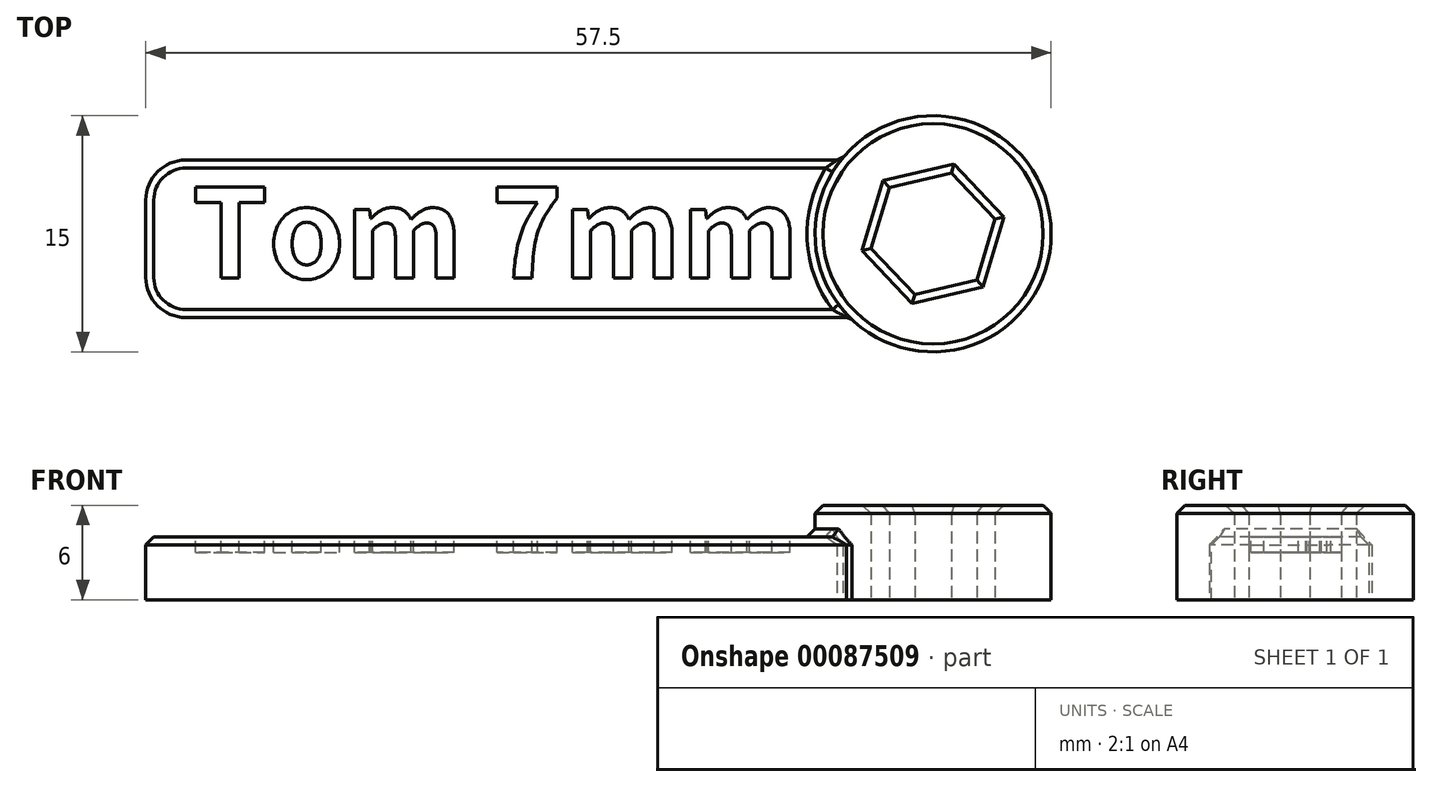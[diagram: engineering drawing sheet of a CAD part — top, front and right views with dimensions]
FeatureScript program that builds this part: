
annotation { "Feature Type Name" : "Feature", "Feature Type Description" : "" }
export const myFeature = defineFeature(function(context is Context, id is Id, definition is map)
    precondition{}
    {
        {
            var Q0;
            Q0=qCreatedBy(makeId("Top.planeOp"),FACE);
            var sketch = newSketch(context, id + "F0", { "sketchPlane" : qUnion([Q0])});
            skCircle(sketch, "E0.cCircle", {"center": v(0, 0) * mm, "radius": 4.04 * mm, "construction": true});
            skLineSegment(sketch, "E0.0", {"start": v(3.93, 0.93) * mm, "end": v(1.16, 3.87) * mm});
            skLineSegment(sketch, "E0.1", {"start": v(2.77, -2.94) * mm, "end": v(3.93, 0.93) * mm});
            skLineSegment(sketch, "E0.2", {"start": v(-1.16, -3.87) * mm, "end": v(2.77, -2.94) * mm});
            skLineSegment(sketch, "E0.3", {"start": v(-3.93, -0.93) * mm, "end": v(-1.16, -3.87) * mm});
            skLineSegment(sketch, "E0.4", {"start": v(-2.77, 2.94) * mm, "end": v(-3.93, -0.93) * mm});
            skLineSegment(sketch, "E0.5", {"start": v(1.16, 3.87) * mm, "end": v(-2.77, 2.94) * mm});
            skCircle(sketch, "E1", {"center": v(0, 0) * mm, "radius": 7.5 * mm});
            skLineSegment(sketch, "E2.bottom", {"start": v(-50, -5.32) * mm, "end": v(-5.29, -5.32) * mm});
            skLineSegment(sketch, "E2.top", {"start": v(-50, 4.68) * mm, "end": v(-5.86, 4.68) * mm});
            skLineSegment(sketch, "E2.left", {"start": v(-50, -5.32) * mm, "end": v(-50, 4.68) * mm});
            skSolve(sketch);
        }
        {
            var Q0;
            Q0=makeQuery(id+"F0.imprint","IMPRINT",FACE,{"disambiguationData":[TD([[makeQuery(id+"F0.imprint","IMPRINT",EDGE,{"derivedFrom":sQuery(id+"F0.wireOp",EDGE,"E0.0")}),-1.0]])]});
            extrude(context, id + "F1", {"entities" : qUnion([Q0]), "depth" : 6 * mm});
        }
        {
            var Q0;
            {var subQ0=sQuery(id+"F0.wireOp",EDGE,"E2.bottom");Q0=makeQuery(id+"F0.imprint","IMPRINT",FACE,{"disambiguationData":[TD([[makeQuery(id+"F0.imprint","IMPRINT",EDGE,{"derivedFrom":subQ0}),1.0]])]});}
            extrude(context, id + "F2", {"entities" : qUnion([Q0]), "operationType" : NewBodyOperationType.ADD, "depth" : 4 * mm});
        }
        {
            var Q0;
            Q0=makeQuery(id+"F2.opExtrude","SWEPT_EDGE",EDGE,{"disambiguationData":[OSD([sQuery(id+"F0.wireOp",EDGE,"E2.bottom"),sQuery(id+"F0.wireOp",EDGE,"E2.left")])]});
            var Q1;
            Q1=makeQuery(id+"F2.opExtrude","SWEPT_EDGE",EDGE,{"disambiguationData":[OSD([sQuery(id+"F0.wireOp",EDGE,"E2.top"),sQuery(id+"F0.wireOp",EDGE,"E2.left")])]});
            fillet(context, id + "F3", {"entities" : qUnion([Q0, Q1]), "radius" : 2.54 * mm, "tangentPropagation" : true, "allowEdgeOverflow" : false});
        }
        {
            var Q0;
            Q0=makeQuery(id+"F1.opExtrude","CAP_FACE",FACE,{"disambiguationData":[OSD([sQuery(id+"F0.wireOp",EDGE,"E0.0"),sQuery(id+"F0.wireOp",EDGE,"E0.1"),sQuery(id+"F0.wireOp",EDGE,"E0.2"),sQuery(id+"F0.wireOp",EDGE,"E0.3"),sQuery(id+"F0.wireOp",EDGE,"E0.4"),sQuery(id+"F0.wireOp",EDGE,"E0.5"),sQuery(id+"F0.wireOp",EDGE,"E1")])],"isStart":false});
            chamfer(context, id + "F4", {"entities" : qUnion([Q0]), "width" : 0.5 * mm, "tangentPropagation" : true});
        }
        {
            var Q0;
            Q0=makeQuery(id+"F2.opExtrude","CAP_FACE",FACE,{"disambiguationData":[OSD([sQuery(id+"F0.wireOp",EDGE,"E1"),sQuery(id+"F0.wireOp",EDGE,"E2.bottom"),sQuery(id+"F0.wireOp",EDGE,"E2.top"),sQuery(id+"F0.wireOp",EDGE,"E2.left")])],"isStart":false});
            chamfer(context, id + "F5", {"entities" : qUnion([Q0]), "width" : 0.5 * mm, "tangentPropagation" : true});
        }
        {
            var Q0;
            Q0=makeQuery(id+"F2.opExtrude","CAP_FACE",FACE,{"disambiguationData":[OSD([sQuery(id+"F0.wireOp",EDGE,"E1"),sQuery(id+"F0.wireOp",EDGE,"E2.bottom"),sQuery(id+"F0.wireOp",EDGE,"E2.top"),sQuery(id+"F0.wireOp",EDGE,"E2.left")])],"isStart":false});
            var sketch = newSketch(context, id + "F6", { "sketchPlane" : qUnion([Q0])});
            skText(sketch, "E3", { "text": "Tom 7mm", "fontName": "NotoSansCJKsc-Bold.otf"});
            const initialGuessF6  = {"E3": [-0.04708, -0.0028, 1, 0, 0.0056]};
            skSetInitialGuess(sketch, initialGuessF6);
            skSolve(sketch);
        }
        {
            var Q0;
            Q0=makeQuery(id+"F6.imprint","IMPRINT",FACE,{"disambiguationData":[TD([[makeQuery(id+"F6.imprint","IMPRINT",EDGE,{"derivedFrom":sQuery(id+"F6.wireOp",EDGE,"E3.sketch_text.stroke-0")}),1.0]])]});
            var Q1;
            Q1=makeQuery(id+"F6.imprint","IMPRINT",FACE,{"disambiguationData":[TD([[makeQuery(id+"F6.imprint","IMPRINT",EDGE,{"derivedFrom":sQuery(id+"F6.wireOp",EDGE,"E3.sketch_text.stroke-16")}),1.0]])]});
            var Q2;
            Q2=makeQuery(id+"F6.imprint","IMPRINT",FACE,{"disambiguationData":[TD([[makeQuery(id+"F6.imprint","IMPRINT",EDGE,{"derivedFrom":sQuery(id+"F6.wireOp",EDGE,"E3.sketch_text.stroke-36")}),1.0]])]});
            var Q3;
            Q3=makeQuery(id+"F6.imprint","IMPRINT",FACE,{"disambiguationData":[TD([[makeQuery(id+"F6.imprint","IMPRINT",EDGE,{"derivedFrom":sQuery(id+"F6.wireOp",EDGE,"E3.sketch_text.stroke-43")}),1.0]])]});
            var Q4;
            Q4=makeQuery(id+"F6.imprint","IMPRINT",FACE,{"disambiguationData":[TD([[makeQuery(id+"F6.imprint","IMPRINT",EDGE,{"derivedFrom":sQuery(id+"F6.wireOp",EDGE,"E3.sketch_text.stroke-63")}),1.0]])]});
            var Q5;
            Q5=makeQuery(id+"F6.imprint","IMPRINT",FACE,{"disambiguationData":[TD([[makeQuery(id+"F6.imprint","IMPRINT",EDGE,{"derivedFrom":sQuery(id+"F6.wireOp",EDGE,"E3.sketch_text.stroke-8")}),1.0]])]});
            extrude(context, id + "F7", {"entities" : qUnion([Q0, Q1, Q2, Q3, Q4, Q5]), "operationType" : NewBodyOperationType.REMOVE, "oppositeDirection" : true, "depth" : 1 * mm});
        }
    });
